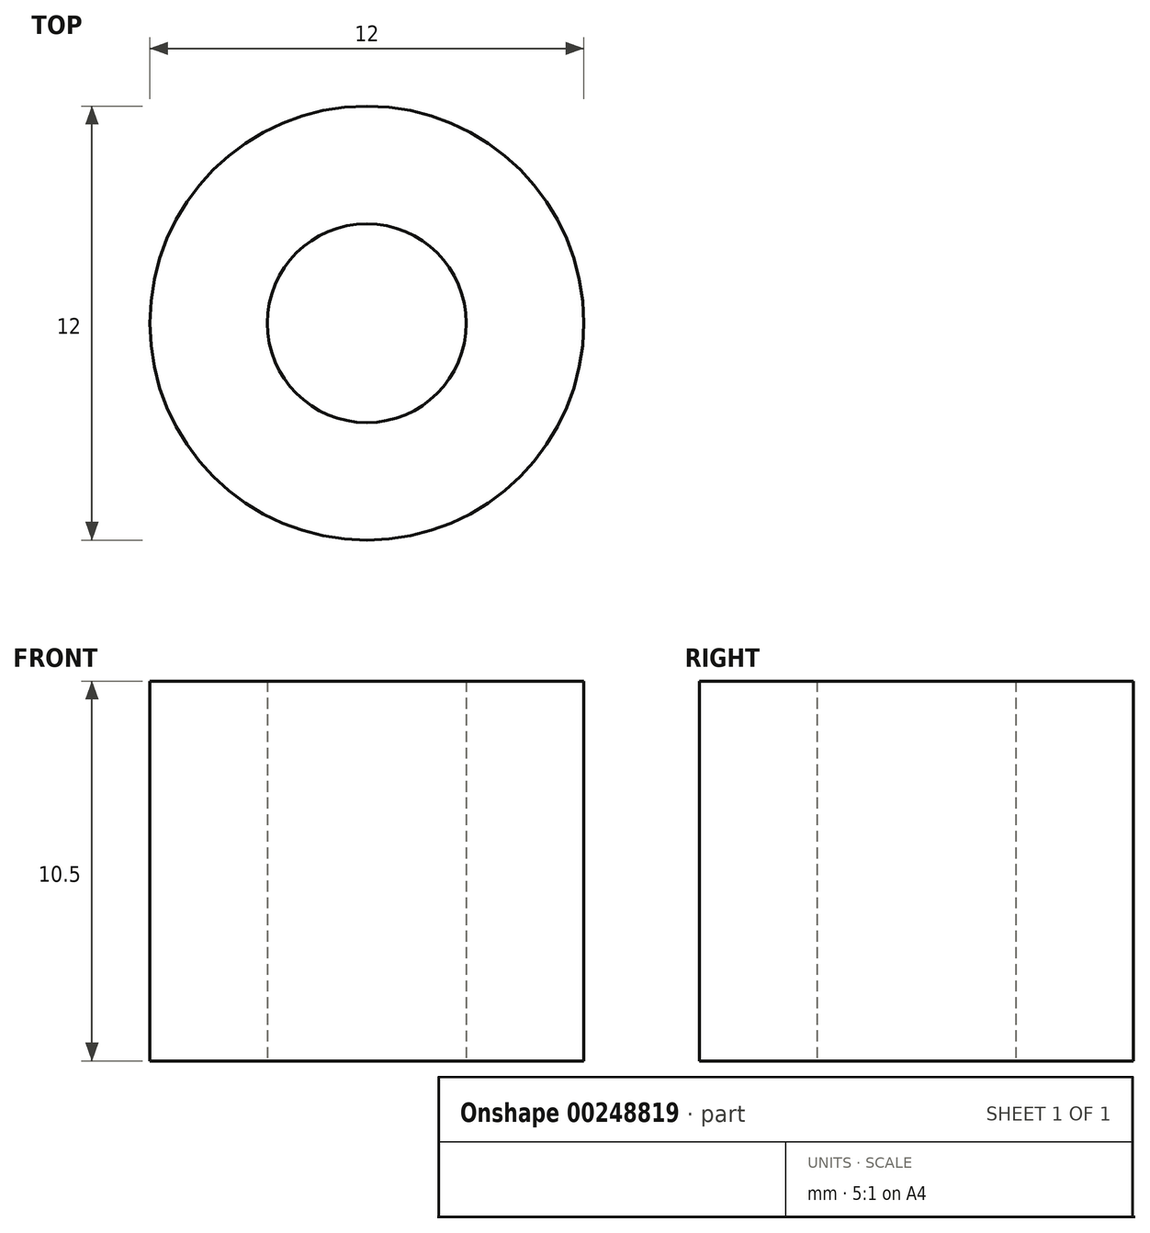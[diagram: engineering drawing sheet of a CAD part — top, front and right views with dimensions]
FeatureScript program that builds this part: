
annotation { "Feature Type Name" : "Feature", "Feature Type Description" : "" }
export const myFeature = defineFeature(function(context is Context, id is Id, definition is map)
    precondition{}
    {
        {
            var Q0;
            Q0=qCreatedBy(makeId("Top.planeOp"),FACE);
            var sketch = newSketch(context, id + "F0", { "sketchPlane" : qUnion([Q0])});
            skCircle(sketch, "E0", {"center": v(0, 0) * mm, "radius": 6 * mm});
            skCircle(sketch, "E1", {"center": v(0, 0) * mm, "radius": 2.75 * mm});
            skSolve(sketch);
        }
        {
            var Q0;
            Q0=makeQuery(id+"F0.imprint","IMPRINT",FACE,{"disambiguationData":[TD([[makeQuery(id+"F0.imprint","IMPRINT",EDGE,{"derivedFrom":sQuery(id+"F0.wireOp",EDGE,"E0")}),1.0]])]});
            extrude(context, id + "F1", {"entities" : qUnion([Q0]), "depth" : 10.5 * mm});
        }
    });
